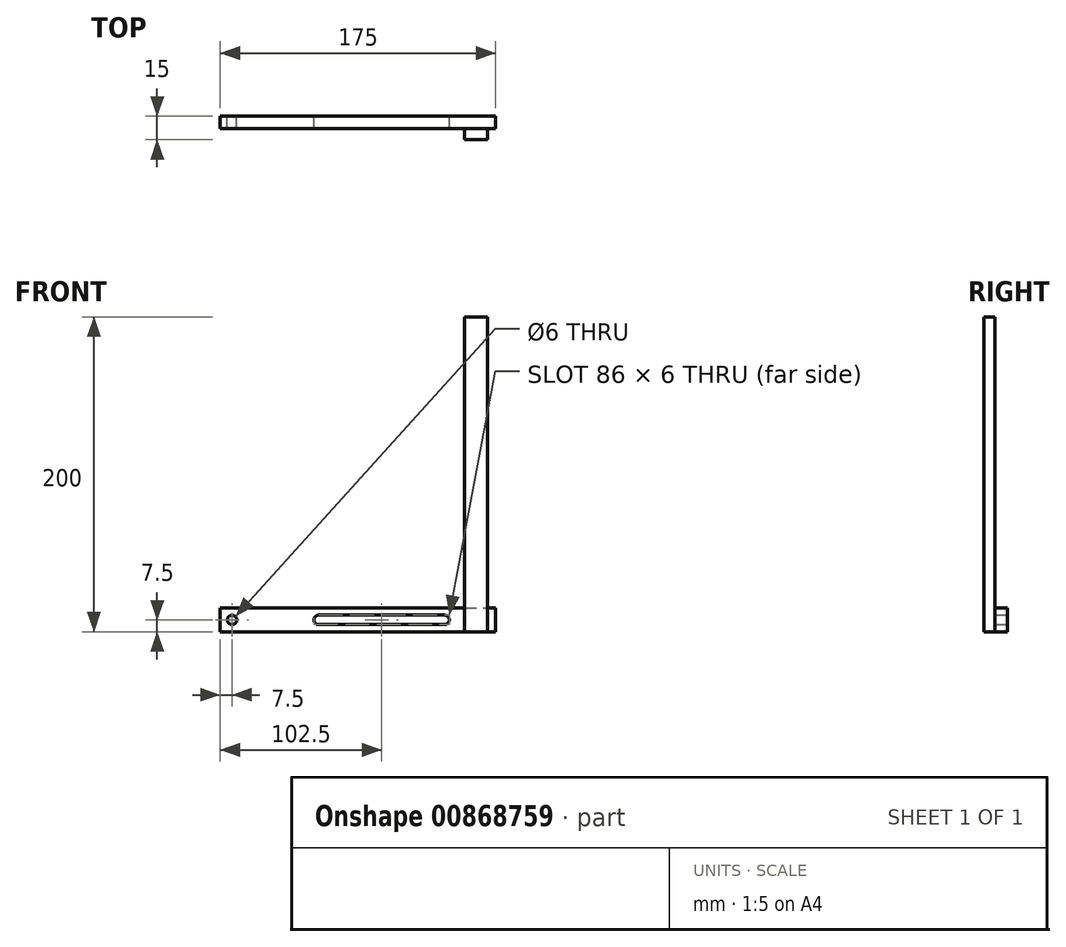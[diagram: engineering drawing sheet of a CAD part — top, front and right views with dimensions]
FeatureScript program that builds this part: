
annotation { "Feature Type Name" : "Feature", "Feature Type Description" : "" }
export const myFeature = defineFeature(function(context is Context, id is Id, definition is map)
    precondition{}
    {
        {
            var Q0;
            Q0=qCreatedBy(makeId("Front.planeOp"),FACE);
            var sketch = newSketch(context, id + "F0", { "sketchPlane" : qUnion([Q0])});
            skCircle(sketch, "E0", {"center": v(0, 0) * mm, "radius": 3 * mm});
            skLineSegment(sketch, "E1.bottom", {"start": v(-7.5, -7.5) * mm, "end": v(142.5, -7.5) * mm});
            skLineSegment(sketch, "E1.top", {"start": v(-7.5, 7.5) * mm, "end": v(142.5, 7.5) * mm});
            skLineSegment(sketch, "E1.left", {"start": v(-7.5, -7.5) * mm, "end": v(-7.5, 7.5) * mm});
            skLineSegment(sketch, "E1.right", {"start": v(142.5, -7.5) * mm, "end": v(142.5, 7.5) * mm});
            skLineSegment(sketch, "E2.bottom", {"start": v(55, 3) * mm, "end": v(135, 3) * mm});
            skLineSegment(sketch, "E2.top", {"start": v(55, -3) * mm, "end": v(135, -3) * mm});
            skArc(sketch, "E3", {"start": v(135, -3) * mm, "mid": v(138, 0) * mm, "end": v(135, 3) * mm});
            skArc(sketch, "E4", {"start": v(55, 3) * mm, "mid": v(52, 0) * mm, "end": v(55, -3) * mm});
            skSolve(sketch);
        }
        {
            var Q0;
            Q0=makeQuery(id+"F0.imprint","IMPRINT",FACE,{"disambiguationData":[TD([[makeQuery(id+"F0.imprint","IMPRINT",EDGE,{"derivedFrom":sQuery(id+"F0.wireOp",EDGE,"E0")}),-1.0]])]});
            extrude(context, id + "F1", {"entities" : qUnion([Q0]), "depth" : 8 * mm, "offsetDistance" : 25 * mm, "symmetric" : true});
        }
        {
            var Q0;
            Q0=makeQuery(id+"F1.opExtrude","SWEPT_FACE",FACE,{"disambiguationData":[OSD([sQuery(id+"F0.wireOp",EDGE,"E1.right")])]});
            var sketch = newSketch(context, id + "F2", { "sketchPlane" : qUnion([Q0])});
            skLineSegment(sketch, "E5.0", {"start": v(-4, -7.5) * mm, "end": v(-4, 7.5) * mm});
            skLineSegment(sketch, "E6.0", {"start": v(4, -7.5) * mm, "end": v(4, 7.5) * mm});
            skLineSegment(sketch, "E7.0", {"start": v(-4, 7.5) * mm, "end": v(4, 7.5) * mm});
            skLineSegment(sketch, "E8.0", {"start": v(-4, -7.5) * mm, "end": v(4, -7.5) * mm});
            skSolve(sketch);
        }
        {
            var Q0;
            Q0=makeQuery(id+"F2.imprint","IMPRINT",FACE,{"disambiguationData":[TD([[makeQuery(id+"F2.imprint","IMPRINT",EDGE,{"derivedFrom":sQuery(id+"F2.wireOp",EDGE,"E5.0")}),-1.0]])]});
            extrude(context, id + "F3", {"entities" : qUnion([Q0]), "operationType" : NewBodyOperationType.ADD, "depth" : 25 * mm, "offsetDistance" : 25 * mm});
        }
        {
            var Q0;
            Q0=makeQuery(id+"F3.boolean.opBoolean","MERGE",FACE,{"derivedFrom":[makeQuery(id+"F1.opExtrude","SWEPT_FACE",FACE,{"disambiguationData":[OSD([sQuery(id+"F0.wireOp",EDGE,"E1.bottom")])]}),makeQuery(id+"F3.opExtrude","SWEPT_FACE",FACE,{"disambiguationData":[OSD([sQuery(id+"F2.wireOp",EDGE,"E8.0")])]})]});
            var sketch = newSketch(context, id + "F4", { "sketchPlane" : qUnion([Q0])});
            skLineSegment(sketch, "E9.0.0", {"start": v(167.5, 4) * mm, "end": v(-7.5, 4) * mm});
            skLineSegment(sketch, "E9.0.2", {"start": v(-7.5, 4) * mm, "end": v(167.5, 4) * mm, "construction": true});
            skLineSegment(sketch, "E10.bottom", {"start": v(162.25, 4) * mm, "end": v(147.75, 4) * mm});
            skLineSegment(sketch, "E10.top", {"start": v(162.25, 11) * mm, "end": v(147.75, 11) * mm});
            skLineSegment(sketch, "E10.left", {"start": v(162.25, 4) * mm, "end": v(162.25, 11) * mm});
            skLineSegment(sketch, "E10.right", {"start": v(147.75, 4) * mm, "end": v(147.75, 11) * mm});
            skLineSegment(sketch, "E11", {"start": v(147.75, 4) * mm, "end": v(162.25, 4) * mm});
            skSolve(sketch);
        }
        {
            var Q0;
            Q0=makeQuery(id+"F4.imprint","IMPRINT",FACE,{"disambiguationData":[TD([[makeQuery(id+"F4.imprint","IMPRINT",EDGE,{"derivedFrom":sQuery(id+"F4.wireOp",EDGE,"E10.top")}),1.0]])]});
            extrude(context, id + "F5", {"entities" : qUnion([Q0]), "operationType" : NewBodyOperationType.ADD, "oppositeDirection" : true, "depth" : 200 * mm, "offsetDistance" : 25 * mm});
        }
    });
